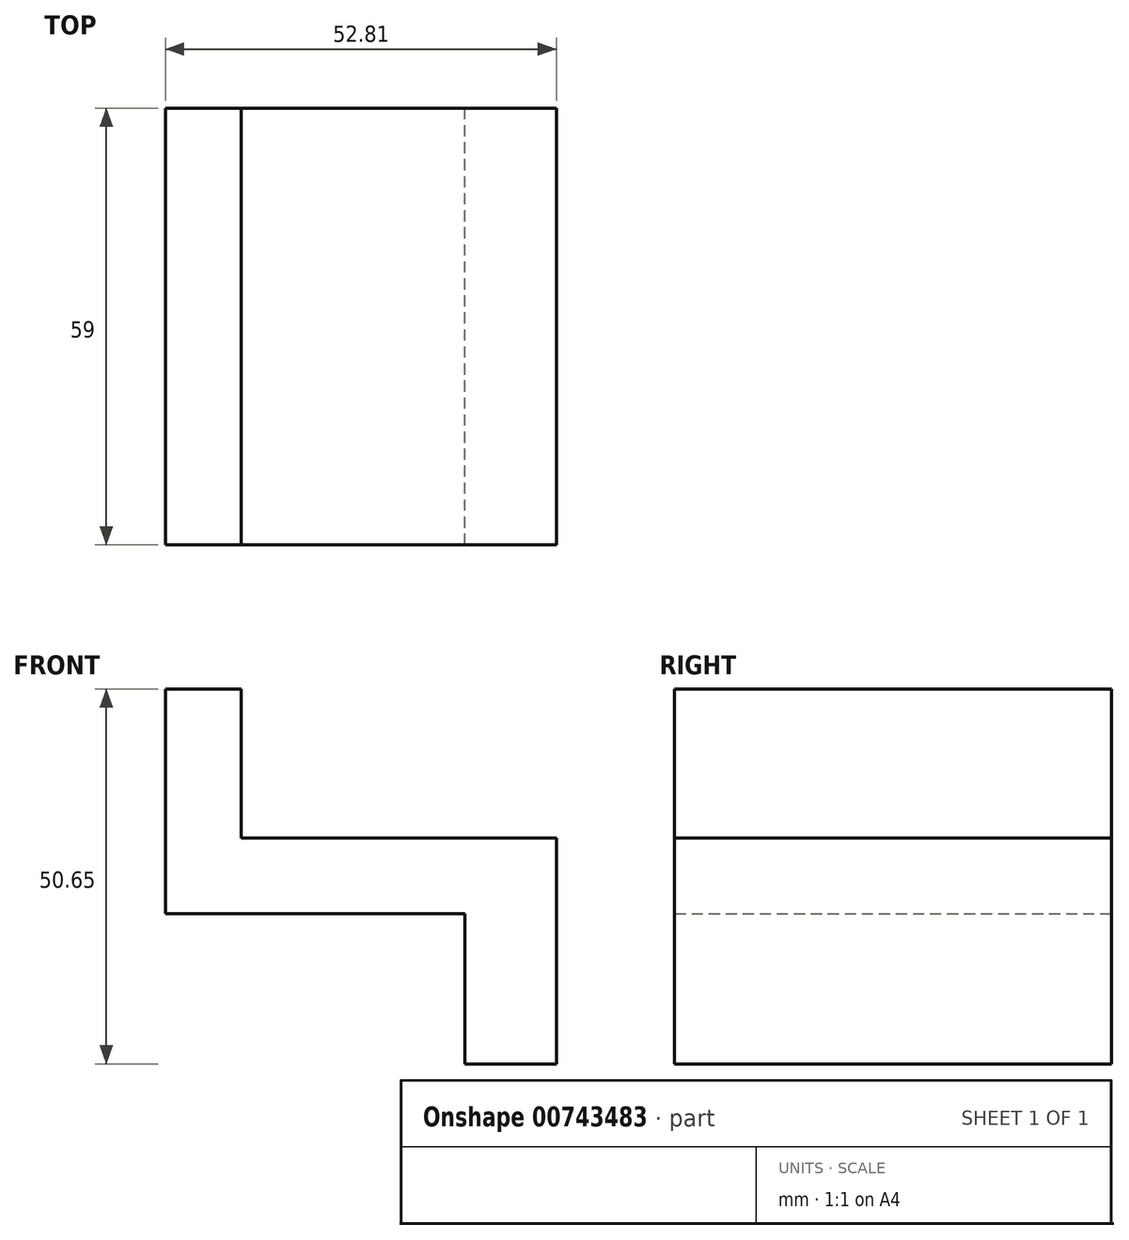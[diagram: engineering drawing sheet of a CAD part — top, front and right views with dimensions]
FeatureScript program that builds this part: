
annotation { "Feature Type Name" : "Feature", "Feature Type Description" : "" }
export const myFeature = defineFeature(function(context is Context, id is Id, definition is map)
    precondition{}
    {
        {
            var Q0;
            Q0=qCreatedBy(makeId("Front.planeOp"),FACE);
            var sketch = newSketch(context, id + "F0", { "sketchPlane" : qUnion([Q0])});
            skLineSegment(sketch, "E0", {"start": v(0, 0) * mm, "end": v(0, 30.36) * mm});
            skLineSegment(sketch, "E1", {"start": v(0, 30.36) * mm, "end": v(10.22, 30.36) * mm});
            skLineSegment(sketch, "E2", {"start": v(0, 0) * mm, "end": v(40.44, 0) * mm});
            skLineSegment(sketch, "E3", {"start": v(10.22, 30.36) * mm, "end": v(10.22, 10.22) * mm});
            skLineSegment(sketch, "E4", {"start": v(10.22, 10.22) * mm, "end": v(52.81, 10.22) * mm});
            skLineSegment(sketch, "E5", {"start": v(52.81, 10.22) * mm, "end": v(52.81, -20.3) * mm});
            skLineSegment(sketch, "E6", {"start": v(52.81, -20.3) * mm, "end": v(40.44, -20.3) * mm});
            skLineSegment(sketch, "E7", {"start": v(40.44, -20.3) * mm, "end": v(40.44, 0) * mm});
            skSolve(sketch);
        }
        {
            var Q0;
            Q0 = qSketchRegion(id + "F0", true);
            extrude(context, id + "F1", {"entities" : qUnion([Q0]), "depth" : 59 * mm, "offsetDistance" : 25 * mm});
        }
    });
